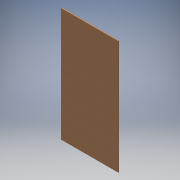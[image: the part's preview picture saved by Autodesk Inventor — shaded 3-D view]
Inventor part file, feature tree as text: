
AUTODESK INVENTOR PART (.ipt)
format: ipt  version: 2017 (Build 210142000, 142)  size: 100,352 bytes
history: native  units: mm
features: reference x3, other x3, extrude x1, sketch x1
ambient origin geometry x8: Origin, YZ Plane, XZ Plane, XY Plane, X Axis, Y Axis, Z Axis, Center Point
bodies: Volumenkörper1 (feature_tree)
feature tree (8):
  extrude  "Extrusion1"  Depth=15.0mm
  sketch  "Skizze1"  dims[d0=20.0mm d1=20.0mm d2=20.0mm d3=15.0mm d4=0.0mm]
  reference  "Referenz1"
  reference  "Referenz2"
  reference  "Referenz3"
  other  "<userpath>\Documents\Inventor\Oli_Grundstück\Tür.iam"
  other  "Tür.iam"
  other  "Rahmen:1"
